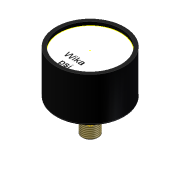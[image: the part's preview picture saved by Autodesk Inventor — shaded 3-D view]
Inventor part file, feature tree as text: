
AUTODESK INVENTOR PART (.ipt)
format: ipt  version: unknown  size: 211,456 bytes
history: native  units: mm (DEFAULTED — no unit token found)
features: sketch x6, extrude x5, thread x1, chamfer x1, fillet x1
ambient origin geometry x8: Origin, YZ Plane, XZ Plane, XY Plane, X Axis, Y Axis, Z Axis, Center Point
feature tree (14):
  extrude  "Extrusion13"  Depth=26.0mm TaperAngle=0.0deg
  extrude  "Extrusion15"  Depth=14.0mm
  extrude  "Extrusion16"  Depth=10.0mm TaperAngle=0.0deg
  thread  "Thread3"  [1 undecoded]
  extrude  "Extrusion18"  Depth=2.0mm
  extrude  "Extrusion19"  Depth=0.5mm TaperAngle=45.0deg
  sketch  "Sketch19"  dims[d67=2.0mm d68=0.0mm d69=0.5mm d70=2.0mm d71=45.0deg]
  chamfer  "Chamfer1"  Distance=10.0mm
  fillet  "Fillet5"  Radius=3.0mm
  sketch  "Sketch13"  dims[d46=40.0mm d47=26.0mm d48=0.0mm]
  sketch  "Sketch15"  dims[d52=14.0mm d53=14.0mm]
  sketch  "Sketch16"  dims[d54=8.0mm d55=0.0mm d56=10.0mm d57=0.0mm d58=9.525mm]
  sketch  "Sketch18"  dims[d59=10.0mm d60=0.0mm d66=2.0mm]
  sketch  "Sketch20"  dims[d72=1.0mm d73=10.0mm d74=0.0mm d75=3.0mm]
note: 1 required parameter value undecoded (feature->parameter linkage not recoverable at this tier; creation-order binding heuristic only, values carry confidence <= 0.55)
